# Revit family: НЕВАТОМ_Дефлектор, версия 1
name_source: partatom
category: Воздухораспределители
revit_build: Autodesk Revit 2017 (Build: 20170118_1100(x64)
units: mm (PartAtom-declared; Revit-internal decimal feet)

## family parameters
Всегда вертикально = Да
На основе рабочей плоскости = Нет
Общий = Нет
При загрузке вырезать с полостями = Нет
Размер круглого соединителя = Использовать диаметр
Тип детали = Нормальный
Точка расчета площади = Нет

## types (18) — shared parameters
ADSK_Единица измерения = шт
ADSK_Завод-изготовитель = НЕВАТОМ
ADSK_Количество = 1
ADSK_Масса_Текст = кг
ADSK_Материал наименование = Оцинкованная сталь
ADSK_Наименование = Дефлектор
ADSK_Потеря давления воздуха = 0.0 Па
ADSK_Расход воздуха = 0.0 л/с
Nevatom_URL = https://t.me
Материал = Материал корпуса

## per-type parameters (varying)
| type | ADSK_Марка | ADSK_Размер_Высота | ADSK_Размер_Длина | ADSK_Размер_Ширина | D | D in | D* | D3 | D3/2 | Н | Н2 |
| 500 | Дефлектор-500 –ОЦ–Н | 850 мм | 1000 мм | 1000 мм | 500 мм | 975 мм | 25 мм | 1000 мм | 500 мм | 850 мм | 610 мм |
| 100 | Дефлектор-100–ОЦ–Н | 170 мм | 178 мм | 178 мм | 100 мм | 173 мм | 5 мм | 178 мм | 89 мм | 170 мм | 145 мм |
| 125 | Дефлектор-125–ОЦ–Н | 213 мм | 225 мм | 225 мм | 125 мм | 219 мм | 6 мм | 225 мм | 113 мм | 213 мм | 170 мм |
| 160 | Дефлектор-160–ОЦ–Н | 272 мм | 320 мм | 320 мм | 160 мм | 312 мм | 8 мм | 320 мм | 160 мм | 272 мм | 220 мм |
| 200 | Дефлектор-200–ОЦ–Н | 340 мм | 400 мм | 400 мм | 200 мм | 390 мм | 10 мм | 400 мм | 200 мм | 340 мм | 260 мм |
| 250 | Дефлектор-250–ОЦ–Н | 425 мм | 500 мм | 500 мм | 250 мм | 488 мм | 13 мм | 500 мм | 250 мм | 425 мм | 300 мм |
| 315 | Дефлектор-315–ОЦ–Н | 536 мм | 630 мм | 630 мм | 315 мм | 614 мм | 16 мм | 630 мм | 315 мм | 536 мм | 400 мм |
| 355 | Дефлектор-355–ОЦ–Н | 604 мм | 710 мм | 710 мм | 355 мм | 692 мм | 18 мм | 710 мм | 355 мм | 604 мм | 445 мм |
| 400 | Дефлектор-400–ОЦ–Н | 680 мм | 800 мм | 800 мм | 400 мм | 780 мм | 20 мм | 800 мм | 400 мм | 680 мм | 500 мм |
| 450 | Дефлектор-450–ОЦ–Н | 765 мм | 900 мм | 900 мм | 450 мм | 878 мм | 23 мм | 900 мм | 450 мм | 765 мм | 560 мм |
| 560 | Дефлектор-560–ОЦ–Н | 952 мм | 1000 мм | 1000 мм | 560 мм | 972 мм | 28 мм | 1000 мм | 500 мм | 952 мм | 610 мм |
| 630 | Дефлектор-630–ОЦ–Н | 1071 мм | 1260 мм | 1260 мм | 630 мм | 1229 мм | 32 мм | 1260 мм | 630 мм | 1071 мм | 775 мм |
| 710 | Дефлектор-710–ОЦ–Н | 1207 мм | 1330 мм | 1330 мм | 710 мм | 1295 мм | 36 мм | 1330 мм | 665 мм | 1207 мм | 870 мм |
| 800 | Дефлектор-800–ОЦ–Н | 1360 мм | 1600 мм | 1600 мм | 800 мм | 1560 мм | 40 мм | 1600 мм | 800 мм | 1360 мм | 1000 мм |
| 900 | Дефлектор-900–ОЦ–Н | 1530 мм | 1800 мм | 1800 мм | 900 мм | 1755 мм | 45 мм | 1800 мм | 900 мм | 1530 мм | 1060 мм |
| 1000 | Дефлектор-1000–ОЦ–Н | 1700 мм | 2000 мм | 2000 мм | 1000 мм | 1950 мм | 50 мм | 2000 мм | 1000 мм | 1700 мм | 1230 мм |
| 1120 | Дефлектор-1120–ОЦ–Н | 1904 мм | 2240 мм | 2240 мм | 1120 мм | 2184 мм | 56 мм | 2240 мм | 1120 мм | 1904 мм | 1345 мм |
| 1250 | Дефлектор-1250–ОЦ–Н | 2125 мм | 2500 мм | 2500 мм | 1250 мм | 2438 мм | 63 мм | 2500 мм | 1250 мм | 2125 мм | 1500 мм |
